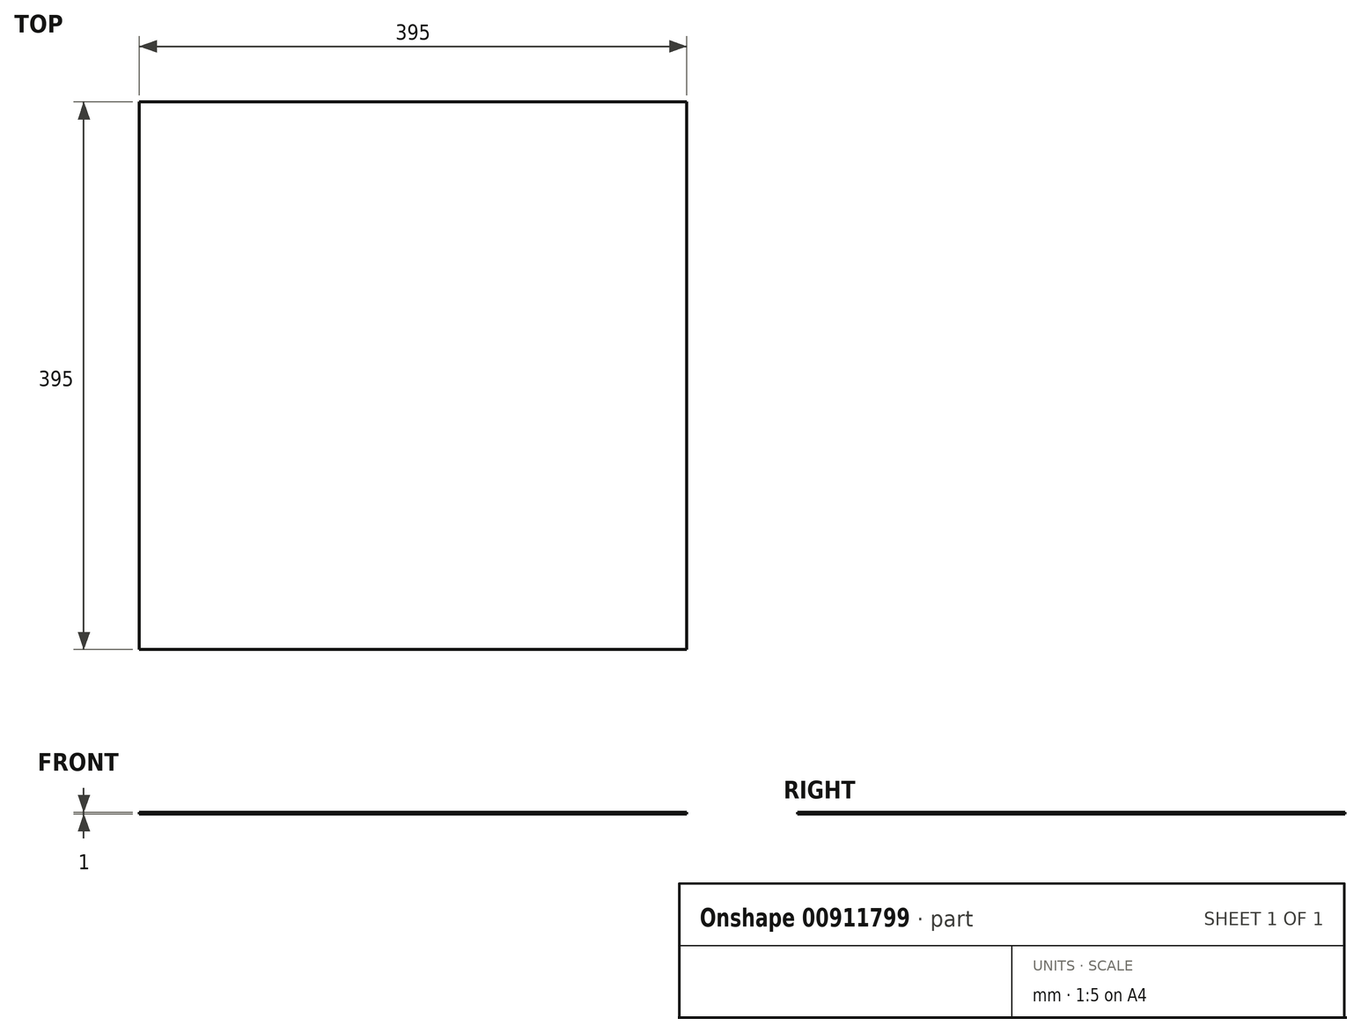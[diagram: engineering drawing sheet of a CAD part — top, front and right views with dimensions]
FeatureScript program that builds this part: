
annotation { "Feature Type Name" : "Feature", "Feature Type Description" : "" }
export const myFeature = defineFeature(function(context is Context, id is Id, definition is map)
    precondition{}
    {
        {
            var Q0;
            Q0=qCreatedBy(makeId("Top.planeOp"),FACE);
            var sketch = newSketch(context, id + "F0", { "sketchPlane" : qUnion([Q0])});
            skLineSegment(sketch, "E0.bottom", {"start": v(-197.5, 197.5) * mm, "end": v(197.5, 197.5) * mm});
            skLineSegment(sketch, "E0.top", {"start": v(-197.5, -197.5) * mm, "end": v(197.5, -197.5) * mm});
            skLineSegment(sketch, "E0.left", {"start": v(-197.5, 197.5) * mm, "end": v(-197.5, -197.5) * mm});
            skLineSegment(sketch, "E0.right", {"start": v(197.5, 197.5) * mm, "end": v(197.5, -197.5) * mm});
            skPoint(sketch, "E0.middle", {"position": v(0, 0) * mm});
            skSolve(sketch);
        }
        {
            var Q0;
            Q0=qSketchRegion(id+"F0",true);
            extrude(context, id + "F1", {"entities" : qUnion([Q0]), "depth" : 1 * mm, "offsetDistance" : 25 * mm});
        }
    });
